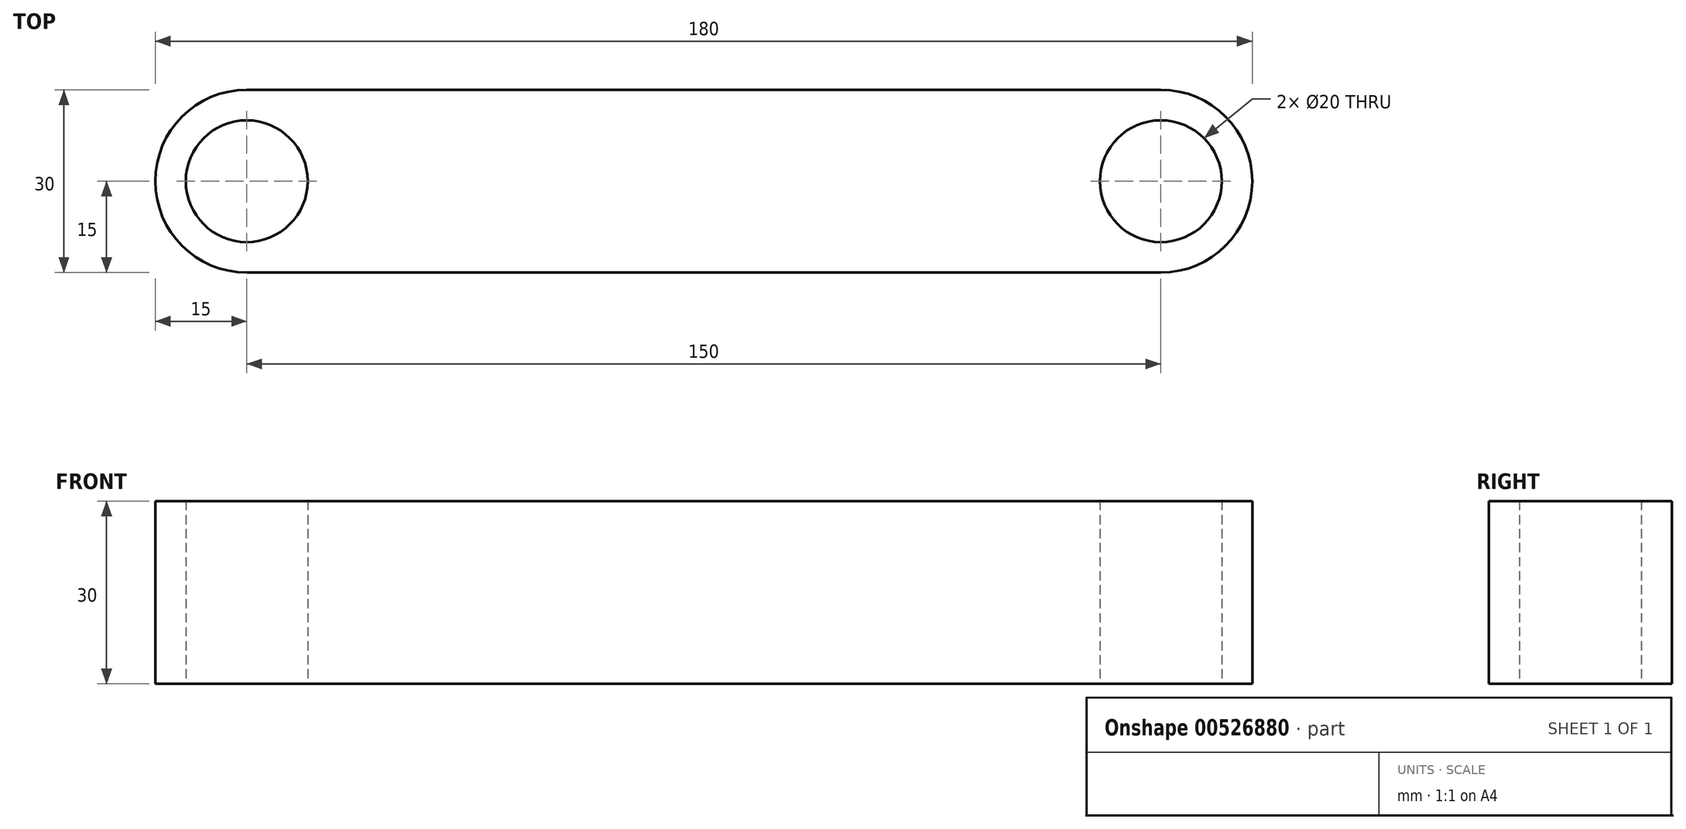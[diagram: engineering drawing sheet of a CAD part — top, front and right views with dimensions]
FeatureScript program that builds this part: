
annotation { "Feature Type Name" : "Feature", "Feature Type Description" : "" }
export const myFeature = defineFeature(function(context is Context, id is Id, definition is map)
    precondition{}
    {
        {
            var Q0;
            Q0=qCreatedBy(makeId("Top.planeOp"),FACE);
            var sketch = newSketch(context, id + "F0", { "sketchPlane" : qUnion([Q0])});
            skLineSegment(sketch, "E0.bottom", {"start": v(75, 15) * mm, "end": v(-75, 15) * mm});
            skLineSegment(sketch, "E0.top", {"start": v(75, -15) * mm, "end": v(-75, -15) * mm});
            skPoint(sketch, "E0.middle", {"position": v(0, 0) * mm});
            skArc(sketch, "E1", {"start": v(-75, 15) * mm, "mid": v(-90, 0) * mm, "end": v(-75, -15) * mm});
            skCircle(sketch, "E2", {"center": v(-75, 0) * mm, "radius": 10 * mm});
            skLineSegment(sketch, "E3", {"start": v(0, 15) * mm, "end": v(0, -15) * mm, "construction": true});
            skArc(sketch, "E4.MirrorCS", {"start": v(75, 15) * mm, "mid": v(90, 0) * mm, "end": v(75, -15) * mm});
            skCircle(sketch, "E5.MirrorC", {"center": v(75, 0) * mm, "radius": 10 * mm});
            skSolve(sketch);
        }
        {
            var Q0;
            Q0=makeQuery(id+"F0.imprint","IMPRINT",FACE,{"disambiguationData":[TD([[makeQuery(id+"F0.imprint","IMPRINT",EDGE,{"derivedFrom":sQuery(id+"F0.wireOp",EDGE,"E0.bottom")}),1.0]])]});
            extrude(context, id + "F1", {"entities" : qUnion([Q0]), "endBound" : BoundingType.SYMMETRIC, "depth" : 10 * mm, "offsetDistance" : 25.4 * mm});
        }
        {
            var Q0;
            Q0=makeQuery(id+"F1.opExtrude","CAP_FACE",FACE,{"disambiguationData":[OSD([sQuery(id+"F0.wireOp",EDGE,"E0.bottom"),sQuery(id+"F0.wireOp",EDGE,"E0.top"),sQuery(id+"F0.wireOp",EDGE,"E1"),sQuery(id+"F0.wireOp",EDGE,"E2"),sQuery(id+"F0.wireOp",EDGE,"E4.MirrorCS"),sQuery(id+"F0.wireOp",EDGE,"E5.MirrorC")])],"isStart":false});
            var sketch = newSketch(context, id + "F2", { "sketchPlane" : qUnion([Q0])});
            skCircle(sketch, "E6", {"center": v(75, 0) * mm, "radius": 10 * mm});
            skSolve(sketch);
        }
        {
            var Q0;
            Q0=makeQuery(id+"F2.imprint","IMPRINT",FACE,{"disambiguationData":[TD([[makeQuery(id+"F2.imprint","IMPRINT",EDGE,{"derivedFrom":sQuery(id+"F2.wireOp",EDGE,"E6")}),-1.0]])]});
            extrude(context, id + "F3", {"entities" : qUnion([Q0]), "operationType" : NewBodyOperationType.ADD, "oppositeDirection" : true, "depth" : 30 * mm, "offsetDistance" : 25.4 * mm});
        }
    });
